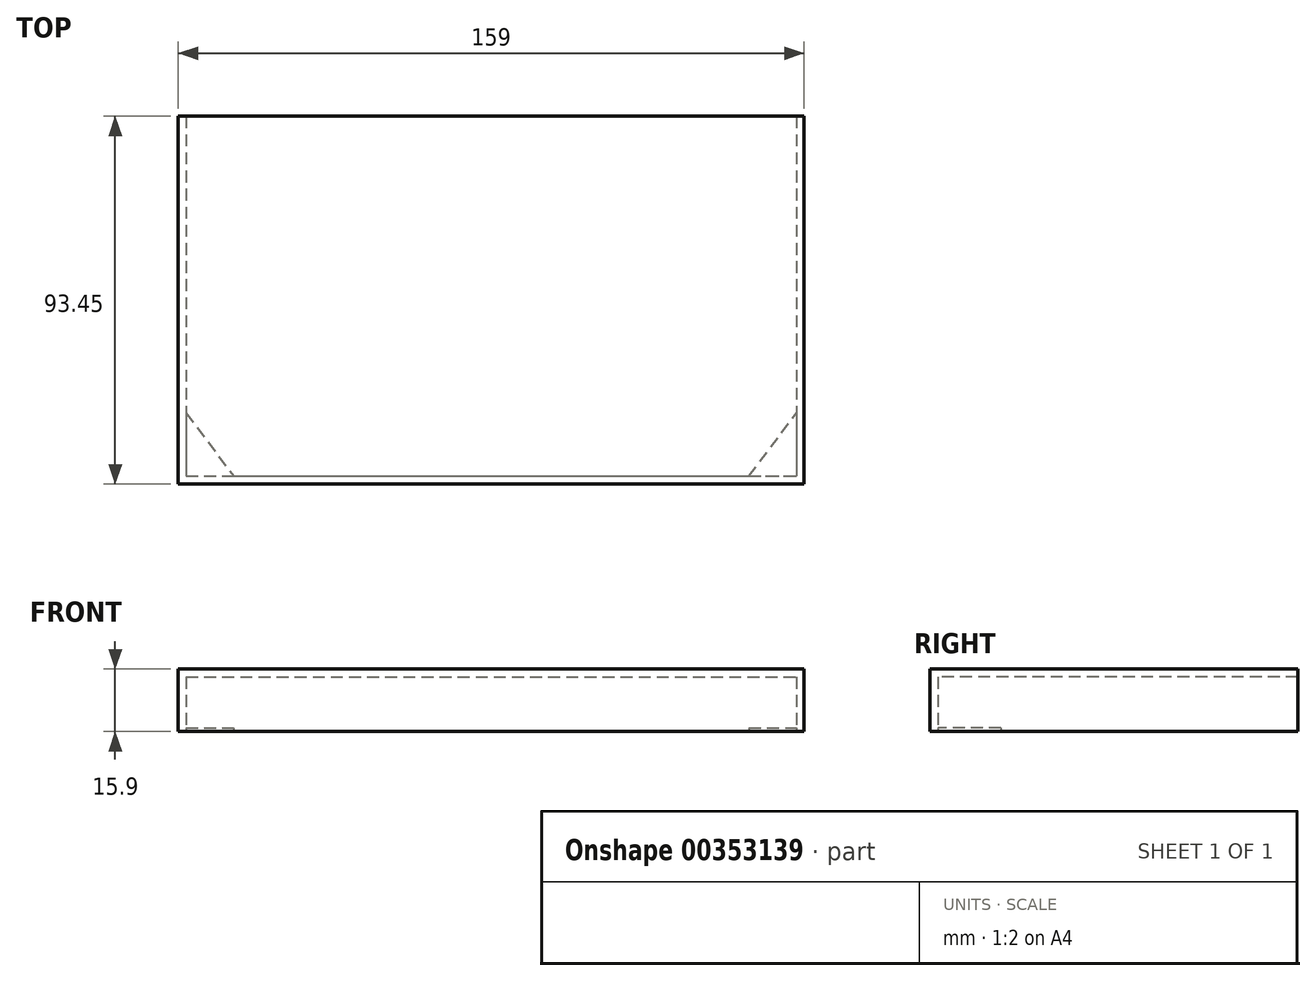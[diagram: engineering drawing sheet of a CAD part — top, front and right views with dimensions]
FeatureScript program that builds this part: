
annotation { "Feature Type Name" : "Feature", "Feature Type Description" : "" }
export const myFeature = defineFeature(function(context is Context, id is Id, definition is map)
    precondition{}
    {
        {
            var Q0;
            Q0=qCreatedBy(makeId("Top.planeOp"),FACE);
            var sketch = newSketch(context, id + "F0", { "sketchPlane" : qUnion([Q0])});
            skLineSegment(sketch, "E0.bottom", {"start": v(-84.82, 44.52) * mm, "end": v(70.18, 44.52) * mm});
            skLineSegment(sketch, "E0.top", {"start": v(-84.82, -46.93) * mm, "end": v(70.18, -46.93) * mm});
            skLineSegment(sketch, "E0.left", {"start": v(-84.82, 44.52) * mm, "end": v(-84.82, -46.93) * mm});
            skLineSegment(sketch, "E0.right", {"start": v(70.18, 44.52) * mm, "end": v(70.18, -46.93) * mm});
            skLineSegment(sketch, "E1.bottom", {"start": v(-86.82, 44.52) * mm, "end": v(72.18, 44.52) * mm});
            skLineSegment(sketch, "E1.top", {"start": v(-86.82, -48.93) * mm, "end": v(72.18, -48.93) * mm});
            skLineSegment(sketch, "E1.left", {"start": v(-86.82, 44.52) * mm, "end": v(-86.82, -48.93) * mm});
            skLineSegment(sketch, "E1.right", {"start": v(72.18, 44.52) * mm, "end": v(72.18, -48.93) * mm});
            skLineSegment(sketch, "E2", {"start": v(-84.82, -30.93) * mm, "end": v(-72.82, -46.93) * mm});
            skLineSegment(sketch, "E3", {"start": v(58.18, -46.93) * mm, "end": v(70.18, -30.93) * mm});
            skSolve(sketch);
        }
        {
            var Q0;
            Q0=makeQuery(id+"F0.imprint","IMPRINT",FACE,{"disambiguationData":[TD([[makeQuery(id+"F0.imprint","IMPRINT",EDGE,{"derivedFrom":sQuery(id+"F0.wireOp",EDGE,"E1.top")}),1.0]])]});
            var Q1;
            {var subQ3=sQuery(id+"F0.wireOp",EDGE,"E2");Q1=makeQuery(id+"F0.imprint","IMPRINT",FACE,{"disambiguationData":[TD([[makeQuery(id+"F0.imprint","IMPRINT",EDGE,{"derivedFrom":subQ3}),-1.0]])]});}
            var Q2;
            {var subQ3=sQuery(id+"F0.wireOp",EDGE,"E3");Q2=makeQuery(id+"F0.imprint","IMPRINT",FACE,{"disambiguationData":[TD([[makeQuery(id+"F0.imprint","IMPRINT",EDGE,{"derivedFrom":subQ3}),-1.0]])]});}
            var Q3;
            {var subQ6=sQuery(id+"F0.wireOp",EDGE,"E2");Q3=makeQuery(id+"F0.imprint","IMPRINT",FACE,{"disambiguationData":[TD([[makeQuery(id+"F0.imprint","IMPRINT",EDGE,{"derivedFrom":subQ6}),1.0]])]});}
            extrude(context, id + "F1", {"entities" : qUnion([Q0, Q1, Q2, Q3]), "depth" : 15.9 * mm});
        }
        {
            var Q0;
            {var subQ3=sQuery(id+"F0.wireOp",EDGE,"E2");Q0=makeQuery(id+"F0.imprint","IMPRINT",FACE,{"disambiguationData":[TD([[makeQuery(id+"F0.imprint","IMPRINT",EDGE,{"derivedFrom":subQ3}),-1.0]])]});}
            var Q1;
            {var subQ6=sQuery(id+"F0.wireOp",EDGE,"E2");Q1=makeQuery(id+"F0.imprint","IMPRINT",FACE,{"disambiguationData":[TD([[makeQuery(id+"F0.imprint","IMPRINT",EDGE,{"derivedFrom":subQ6}),1.0]])]});}
            var Q2;
            {var subQ3=sQuery(id+"F0.wireOp",EDGE,"E3");Q2=makeQuery(id+"F0.imprint","IMPRINT",FACE,{"disambiguationData":[TD([[makeQuery(id+"F0.imprint","IMPRINT",EDGE,{"derivedFrom":subQ3}),-1.0]])]});}
            extrude(context, id + "F2", {"entities" : qUnion([Q0, Q1, Q2]), "operationType" : NewBodyOperationType.REMOVE, "depth" : 13.9 * mm});
        }
        {
            var Q0;
            {var subQ3=sQuery(id+"F0.wireOp",EDGE,"E2");Q0=makeQuery(id+"F0.imprint","IMPRINT",FACE,{"disambiguationData":[TD([[makeQuery(id+"F0.imprint","IMPRINT",EDGE,{"derivedFrom":subQ3}),-1.0]])]});}
            var Q1;
            {var subQ3=sQuery(id+"F0.wireOp",EDGE,"E3");Q1=makeQuery(id+"F0.imprint","IMPRINT",FACE,{"disambiguationData":[TD([[makeQuery(id+"F0.imprint","IMPRINT",EDGE,{"derivedFrom":subQ3}),-1.0]])]});}
            extrude(context, id + "F3", {"entities" : qUnion([Q0, Q1]), "operationType" : NewBodyOperationType.ADD, "depth" : 1 * mm});
        }
    });
